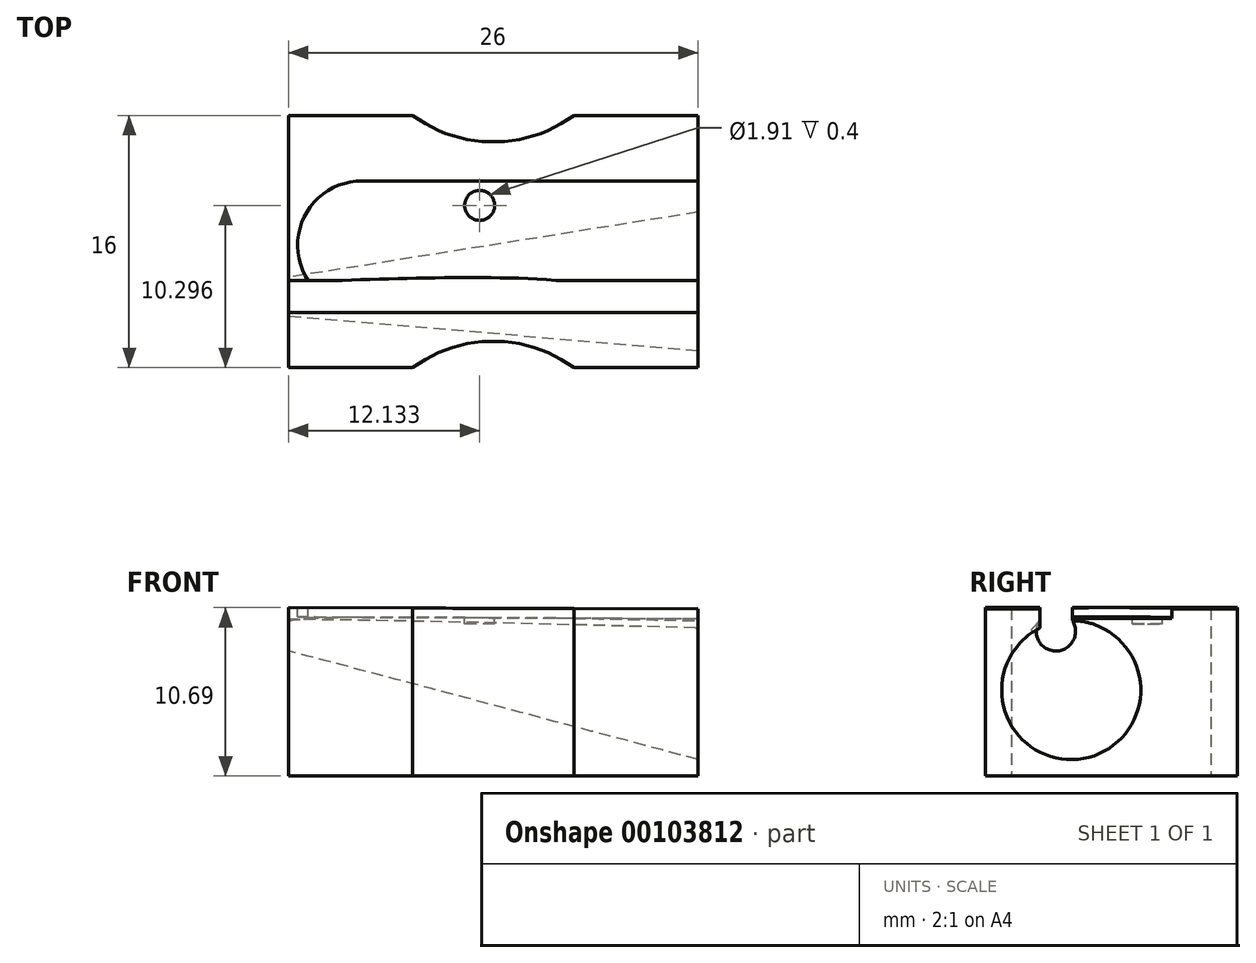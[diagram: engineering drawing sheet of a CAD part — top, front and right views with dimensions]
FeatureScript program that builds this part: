
annotation { "Feature Type Name" : "Feature", "Feature Type Description" : "" }
export const myFeature = defineFeature(function(context is Context, id is Id, definition is map)
    precondition{}
    {
        {
            var Q0;
            Q0=qCreatedBy(makeId("Front.planeOp"),FACE);
            var sketch = newSketch(context, id + "F0", { "sketchPlane" : qUnion([Q0])});
            skLineSegment(sketch, "E0", {"start": v(0, 10.6) * mm, "end": v(0, 0) * mm});
            skLineSegment(sketch, "E1", {"start": v(0, 0) * mm, "end": v(-26, 0) * mm});
            skLineSegment(sketch, "E2", {"start": v(-26, 0) * mm, "end": v(-26, 10.69) * mm});
            skLineSegment(sketch, "E3", {"start": v(-26, 10.69) * mm, "end": v(0, 10.6) * mm});
            skSolve(sketch);
        }
        {
            var Q0;
            Q0=makeQuery(id+"F0.imprint","IMPRINT",FACE,{"disambiguationData":[TD([[makeQuery(id+"F0.imprint","IMPRINT",EDGE,{"derivedFrom":sQuery(id+"F0.wireOp",EDGE,"E0")}),-1.0]])]});
            extrude(context, id + "F1", {"entities" : qUnion([Q0]), "depth" : 16 * mm});
        }
        {
            var Q0;
            Q0=qCreatedBy(makeId("Front.planeOp"),FACE);
            cPlane(context, id + "F2", {"entities" : qUnion([Q0]), "cplaneType" : CPlaneType.OFFSET, "offset" : 10.4 * mm, "width" : 150 * mm, "height" : 150 * mm});
        }
        {
            var Q0;
            Q0=makeQuery(id+"F1.opExtrude","SWEPT_FACE",FACE,{"disambiguationData":[OSD([sQuery(id+"F0.wireOp",EDGE,"E0")])]});
            var sketch = newSketch(context, id + "F3", { "sketchPlane" : qUnion([Q0])});
            skCircle(sketch, "E4", {"center": v(-10.54, 5.45) * mm, "radius": 4.42 * mm});
            skSolve(sketch);
        }
        {
            var Q0;
            Q0=makeQuery(id+"F1.opExtrude","SWEPT_FACE",FACE,{"disambiguationData":[OSD([sQuery(id+"F0.wireOp",EDGE,"E3")])]});
            var sketch = newSketch(context, id + "F4", { "sketchPlane" : qUnion([Q0])});
            skLineSegment(sketch, "E5", {"start": v(-21.36, -4.14) * mm, "end": v(-0.04, -4.14) * mm});
            skLineSegment(sketch, "E6", {"start": v(-0.04, -4.14) * mm, "end": v(-0.04, -12.34) * mm});
            skLineSegment(sketch, "E7", {"start": v(-0.04, -12.34) * mm, "end": v(-21.36, -12.34) * mm});
            skArc(sketch, "E8", {"start": v(-21.36, -4.14) * mm, "mid": v(-25.46, -8.24) * mm, "end": v(-21.36, -12.34) * mm});
            skLineSegment(sketch, "E9", {"start": v(-24.8, -10.47) * mm, "end": v(-0.04, -10.47) * mm});
            skSolve(sketch);
        }
        {
            var Q0;
            {var subQ0=sQuery(id+"F4.wireOp",EDGE,"E5");Q0=makeQuery(id+"F4.imprint","IMPRINT",FACE,{"disambiguationData":[TD([[makeQuery(id+"F4.imprint","IMPRINT",EDGE,{"derivedFrom":subQ0}),-1.0]])]});}
            extrude(context, id + "F5", {"entities" : qUnion([Q0]), "operationType" : NewBodyOperationType.REMOVE, "oppositeDirection" : true, "depth" : 0.6 * mm});
        }
        {
            var Q0;
            Q0=makeQuery(id+"F1.opExtrude","SWEPT_FACE",FACE,{"disambiguationData":[OSD([sQuery(id+"F0.wireOp",EDGE,"E2")])]});
            var sketch = newSketch(context, id + "F6", { "sketchPlane" : qUnion([Q0])});
            skCircle(sketch, "E10", {"center": v(11.52, 9.18) * mm, "radius": 1.25 * mm});
            skSolve(sketch);
        }
        {
            var Q1;
            Q1 = qSketchRegion(id + "F6", true);
            var Q2;
            Q2 = qSketchRegion(id + "F3", true);
            loft(context, id + "F7", {"operationType" : NewBodyOperationType.REMOVE, "sheetProfilesArray" : [{ "sheetProfileEntities" : qUnion([Q1]) }, { "sheetProfileEntities" : qUnion([Q2]) }]});
        }
        {
            var Q0;
            Q0=makeQuery(id+"F1.opExtrude","SWEPT_FACE",FACE,{"disambiguationData":[OSD([sQuery(id+"F0.wireOp",EDGE,"E3")])]});
            var sketch = newSketch(context, id + "F8", { "sketchPlane" : qUnion([Q0])});
            skLineSegment(sketch, "E11", {"start": v(-26.04, -10.47) * mm, "end": v(-0.04, -10.47) * mm});
            skLineSegment(sketch, "E12", {"start": v(-0.04, -10.47) * mm, "end": v(-0.04, -12.52) * mm});
            skLineSegment(sketch, "E13", {"start": v(-0.04, -12.52) * mm, "end": v(-26.04, -12.52) * mm});
            skLineSegment(sketch, "E14", {"start": v(-26.04, -12.52) * mm, "end": v(-26.04, -10.47) * mm});
            skSolve(sketch);
        }
        {
            var Q0;
            {var subQ0=sQuery(id+"F8.wireOp",EDGE,"E12");Q0=makeQuery(id+"F8.imprint","IMPRINT",FACE,{"disambiguationData":[TD([[makeQuery(id+"F8.imprint","IMPRINT",EDGE,{"derivedFrom":subQ0}),1.0]])]});}
            extrude(context, id + "F9", {"entities" : qUnion([Q0]), "operationType" : NewBodyOperationType.REMOVE, "oppositeDirection" : true, "depth" : 1.2 * mm});
        }
        {
            var Q0;
            Q0=makeQuery(id+"F5.boolean.opBoolean","COPY",FACE,{"derivedFrom":makeQuery(id+"F5.opExtrude","CAP_FACE",FACE,{"disambiguationData":[OSD([sQuery(id+"F4.wireOp",EDGE,"E5"),sQuery(id+"F4.wireOp",EDGE,"E6"),sQuery(id+"F4.wireOp",EDGE,"E8"),sQuery(id+"F4.wireOp",EDGE,"E9")])],"isStart":false})});
            var sketch = newSketch(context, id + "F10", { "sketchPlane" : qUnion([Q0])});
            skCircle(sketch, "E15", {"center": v(-13.9, -5.7) * mm, "radius": 0.95 * mm});
            skSolve(sketch);
        }
        {
            var Q0;
            Q0 = qSketchRegion(id + "F10", true);
            extrude(context, id + "F11", {"entities" : qUnion([Q0]), "operationType" : NewBodyOperationType.REMOVE, "oppositeDirection" : true, "depth" : 0.4 * mm});
        }
        {
            var Q0;
            Q0=makeQuery(id+"F1.opExtrude","SWEPT_FACE",FACE,{"disambiguationData":[OSD([sQuery(id+"F0.wireOp",EDGE,"E1")])]});
            var sketch = newSketch(context, id + "F12", { "sketchPlane" : qUnion([Q0])});
            skArc(sketch, "E16", {"start": v(-18.12, 16) * mm, "mid": v(-13, 14.33) * mm, "end": v(-7.88, 16) * mm});
            skArc(sketch, "E17", {"start": v(-7.88, 0) * mm, "mid": v(-13, 1.67) * mm, "end": v(-18.12, 0) * mm});
            skPoint(sketch, "E18", {"position": v(-13, 16) * mm});
            skLineSegment(sketch, "E19", {"start": v(-18.12, 16) * mm, "end": v(-7.88, 16) * mm});
            skLineSegment(sketch, "E20", {"start": v(-18.12, 0) * mm, "end": v(-7.88, 0) * mm});
            skSolve(sketch);
        }
        {
            var Q0;
            Q0=makeQuery(id+"F12.imprint","IMPRINT",FACE,{"disambiguationData":[TD([[makeQuery(id+"F12.imprint","IMPRINT",EDGE,{"derivedFrom":sQuery(id+"F12.wireOp",EDGE,"E17")}),1.0]])]});
            var Q1;
            Q1=makeQuery(id+"F12.imprint","IMPRINT",FACE,{"disambiguationData":[TD([[makeQuery(id+"F12.imprint","IMPRINT",EDGE,{"derivedFrom":sQuery(id+"F12.wireOp",EDGE,"E16")}),1.0]])]});
            extrude(context, id + "F13", {"entities" : qUnion([Q0, Q1]), "operationType" : NewBodyOperationType.REMOVE, "oppositeDirection" : true, "depth" : 13 * mm});
        }
    });
